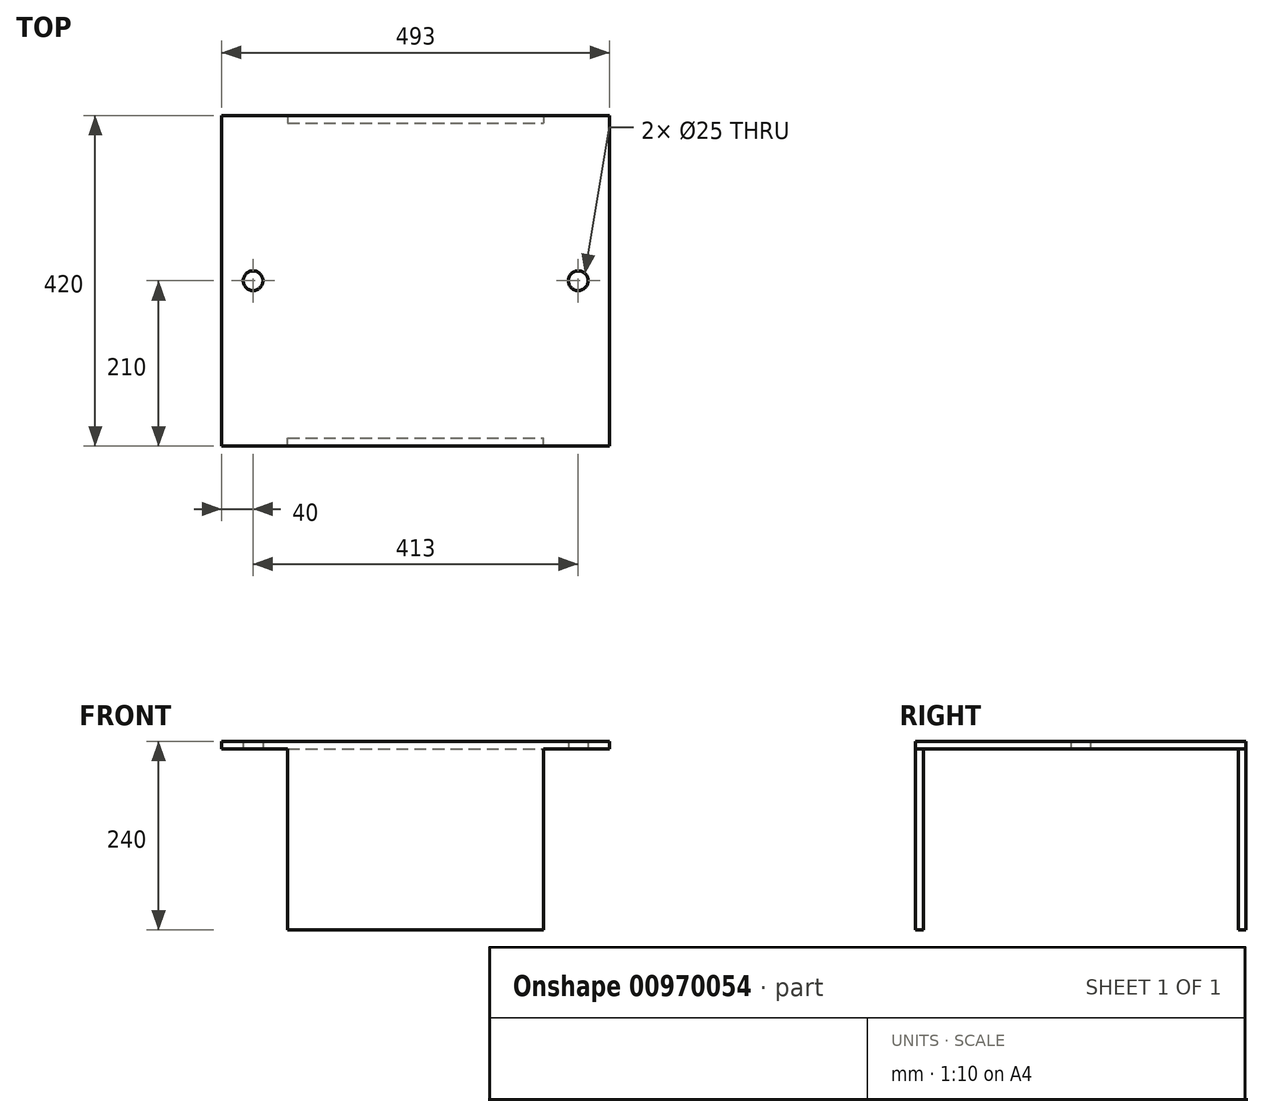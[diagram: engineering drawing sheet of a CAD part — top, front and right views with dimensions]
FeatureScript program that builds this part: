
annotation { "Feature Type Name" : "Feature", "Feature Type Description" : "" }
export const myFeature = defineFeature(function(context is Context, id is Id, definition is map)
    precondition{}
    {
        {
            var Q0;
            Q0=qCreatedBy(makeId("Top.planeOp"),FACE);
            var sketch = newSketch(context, id + "F0", { "sketchPlane" : qUnion([Q0])});
            skLineSegment(sketch, "E0.bottom", {"start": v(0, 0) * mm, "end": v(493, 0) * mm});
            skLineSegment(sketch, "E0.top", {"start": v(0, 420) * mm, "end": v(493, 420) * mm});
            skLineSegment(sketch, "E0.left", {"start": v(0, 0) * mm, "end": v(0, 420) * mm});
            skLineSegment(sketch, "E0.right", {"start": v(493, 0) * mm, "end": v(493, 420) * mm});
            skCircle(sketch, "E1", {"center": v(40, 210) * mm, "radius": 12.5 * mm});
            skLineSegment(sketch, "E2", {"start": v(40, 210) * mm, "end": v(0, 210) * mm, "construction": true});
            skLineSegment(sketch, "E3", {"start": v(40, 210) * mm, "end": v(40, 0) * mm, "construction": true});
            skCircle(sketch, "E4", {"center": v(453, 210) * mm, "radius": 12.5 * mm});
            skLineSegment(sketch, "E5", {"start": v(453, 210) * mm, "end": v(493, 210) * mm, "construction": true});
            skLineSegment(sketch, "E6", {"start": v(453, 210) * mm, "end": v(453, 0) * mm, "construction": true});
            skSolve(sketch);
        }
        {
            var Q0;
            Q0=makeQuery(id+"F0.imprint","IMPRINT",FACE,{"disambiguationData":[TD([[makeQuery(id+"F0.imprint","IMPRINT",EDGE,{"derivedFrom":sQuery(id+"F0.wireOp",EDGE,"E0.bottom")}),1.0]])]});
            extrude(context, id + "F1", {"entities" : qUnion([Q0]), "depth" : 10 * mm, "offsetDistance" : 25 * mm});
        }
        {
            var Q0;
            Q0=makeQuery(id+"F1.opExtrude","CAP_FACE",FACE,{"disambiguationData":[OSD([sQuery(id+"F0.wireOp",EDGE,"E0.bottom"),sQuery(id+"F0.wireOp",EDGE,"E0.top"),sQuery(id+"F0.wireOp",EDGE,"E0.left"),sQuery(id+"F0.wireOp",EDGE,"E0.right"),sQuery(id+"F0.wireOp",EDGE,"E1"),sQuery(id+"F0.wireOp",EDGE,"E4")])],"isStart":true});
            var sketch = newSketch(context, id + "F2", { "sketchPlane" : qUnion([Q0])});
            skLineSegment(sketch, "E7.bottom", {"start": v(84, 0) * mm, "end": v(409, 0) * mm});
            skLineSegment(sketch, "E7.top", {"start": v(84, -10) * mm, "end": v(409, -10) * mm});
            skLineSegment(sketch, "E7.left", {"start": v(84, 0) * mm, "end": v(84, -10) * mm});
            skLineSegment(sketch, "E7.right", {"start": v(409, 0) * mm, "end": v(409, -10) * mm});
            skLineSegment(sketch, "E8", {"start": v(409, -10) * mm, "end": v(493, -10) * mm, "construction": true});
            skLineSegment(sketch, "E9.bottom", {"start": v(84, -420) * mm, "end": v(409, -420) * mm});
            skLineSegment(sketch, "E9.top", {"start": v(84, -410) * mm, "end": v(409, -410) * mm});
            skLineSegment(sketch, "E9.left", {"start": v(84, -420) * mm, "end": v(84, -410) * mm});
            skLineSegment(sketch, "E9.right", {"start": v(409, -420) * mm, "end": v(409, -410) * mm});
            skLineSegment(sketch, "E10", {"start": v(409, -410) * mm, "end": v(493, -410) * mm, "construction": true});
            skSolve(sketch);
        }
        {
            var Q0;
            Q0 = qSketchRegion(id + "F2", true);
            extrude(context, id + "F3", {"entities" : qUnion([Q0]), "operationType" : NewBodyOperationType.ADD, "depth" : 230 * mm, "offsetDistance" : 25 * mm});
        }
    });
